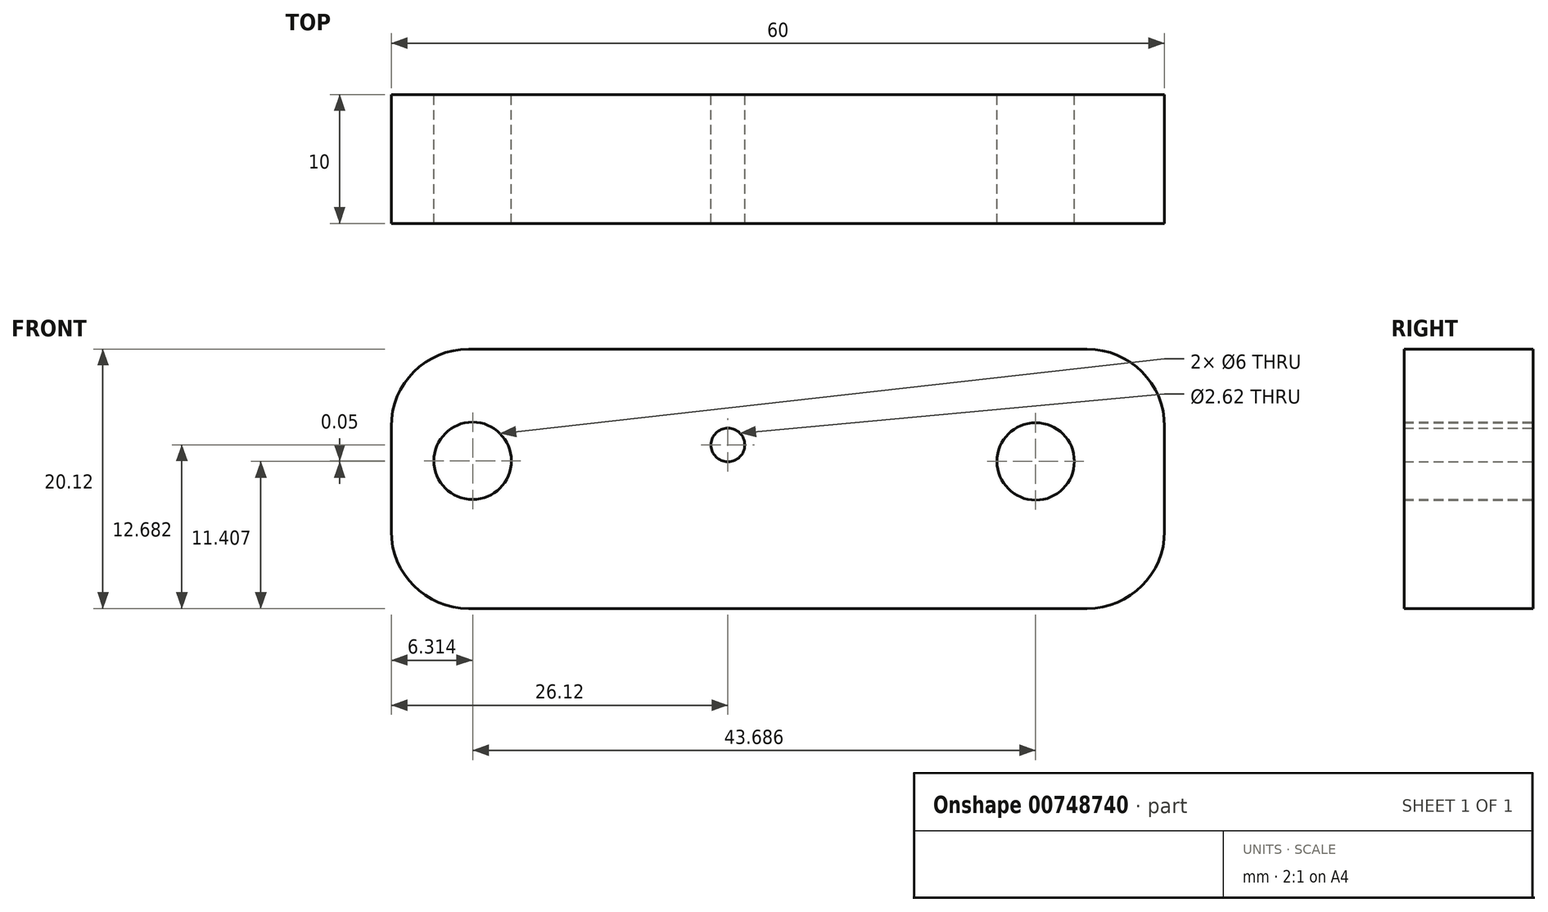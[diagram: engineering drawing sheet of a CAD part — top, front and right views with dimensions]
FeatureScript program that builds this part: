
annotation { "Feature Type Name" : "Feature", "Feature Type Description" : "" }
export const myFeature = defineFeature(function(context is Context, id is Id, definition is map)
    precondition{}
    {
        {
            var Q0;
            Q0=qCreatedBy(makeId("Front.planeOp"),FACE);
            var sketch = newSketch(context, id + "F0", { "sketchPlane" : qUnion([Q0])});
            skLineSegment(sketch, "E0.bottom", {"start": v(0, 0) * mm, "end": v(60, 0) * mm});
            skLineSegment(sketch, "E0.top", {"start": v(0, 20.12) * mm, "end": v(60, 20.12) * mm});
            skLineSegment(sketch, "E0.left", {"start": v(0, 0) * mm, "end": v(0, 20.12) * mm});
            skLineSegment(sketch, "E0.right", {"start": v(60, 0) * mm, "end": v(60, 20.12) * mm});
            skCircle(sketch, "E1", {"center": v(6.31, 11.46) * mm, "radius": 3 * mm});
            skCircle(sketch, "E2", {"center": v(50, 11.4) * mm, "radius": 3 * mm});
            skCircle(sketch, "E3", {"center": v(26.12, 12.68) * mm, "radius": 1.3 * mm});
            skSolve(sketch);
        }
        {
            var Q0;
            Q0=makeQuery(id+"F0.imprint","IMPRINT",FACE,{"disambiguationData":[TD([[makeQuery(id+"F0.imprint","IMPRINT",EDGE,{"derivedFrom":sQuery(id+"F0.wireOp",EDGE,"E0.bottom")}),1.0]])]});
            extrude(context, id + "F1", {"entities" : qUnion([Q0]), "depth" : 10 * mm});
        }
        {
            var Q0;
            Q0=makeQuery(id+"F1.opExtrude","CAP_FACE",FACE,{"disambiguationData":[OSD([sQuery(id+"F0.wireOp",EDGE,"E0.bottom"),sQuery(id+"F0.wireOp",EDGE,"E0.top"),sQuery(id+"F0.wireOp",EDGE,"E0.left"),sQuery(id+"F0.wireOp",EDGE,"E0.right"),sQuery(id+"F0.wireOp",EDGE,"E1"),sQuery(id+"F0.wireOp",EDGE,"E2"),sQuery(id+"F0.wireOp",EDGE,"E3")])],"isStart":true});
            var sketch = newSketch(context, id + "F2", { "sketchPlane" : qUnion([Q0])});
            skLineSegment(sketch, "E4.bottom", {"start": v(-18.36, 10) * mm, "end": v(-20.17, 10) * mm});
            skLineSegment(sketch, "E4.top", {"start": v(-18.36, 7.06) * mm, "end": v(-20.17, 7.06) * mm});
            skLineSegment(sketch, "E4.left", {"start": v(-18.36, 10) * mm, "end": v(-18.36, 7.06) * mm});
            skLineSegment(sketch, "E4.right", {"start": v(-20.17, 10) * mm, "end": v(-20.17, 7.06) * mm});
            skSolve(sketch);
        }
        {
            var Q0;
            Q0=makeQuery(id+"F1.opExtrude","SWEPT_EDGE",EDGE,{"disambiguationData":[OSD([sQuery(id+"F0.wireOp",EDGE,"E0.bottom"),sQuery(id+"F0.wireOp",EDGE,"E0.left")])]});
            var Q1;
            Q1=makeQuery(id+"F1.opExtrude","SWEPT_EDGE",EDGE,{"disambiguationData":[OSD([sQuery(id+"F0.wireOp",EDGE,"E0.top"),sQuery(id+"F0.wireOp",EDGE,"E0.left")])]});
            var Q2;
            Q2=makeQuery(id+"F1.opExtrude","SWEPT_EDGE",EDGE,{"disambiguationData":[OSD([sQuery(id+"F0.wireOp",EDGE,"E0.bottom"),sQuery(id+"F0.wireOp",EDGE,"E0.right")])]});
            var Q3;
            Q3=makeQuery(id+"F1.opExtrude","SWEPT_EDGE",EDGE,{"disambiguationData":[OSD([sQuery(id+"F0.wireOp",EDGE,"E0.top"),sQuery(id+"F0.wireOp",EDGE,"E0.right")])]});
            fillet(context, id + "F3", {"entities" : qUnion([Q0, Q1, Q2, Q3]), "radius" : 6 * mm, "tangentPropagation" : true, "allowEdgeOverflow" : false});
        }
    });
